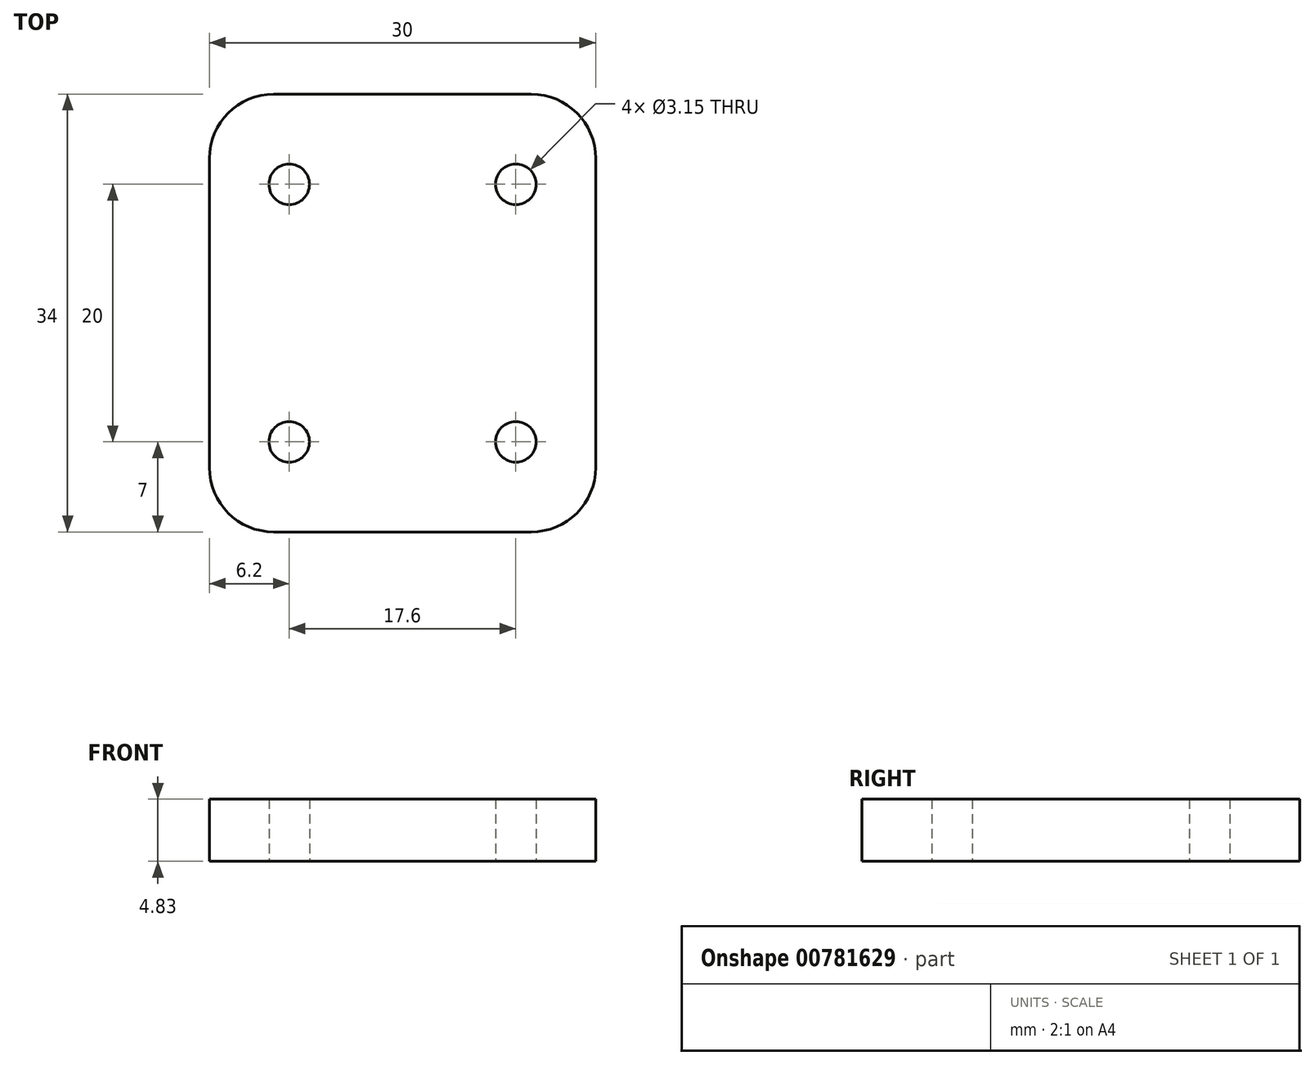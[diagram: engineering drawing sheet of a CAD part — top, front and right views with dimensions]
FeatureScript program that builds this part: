
annotation { "Feature Type Name" : "Feature", "Feature Type Description" : "" }
export const myFeature = defineFeature(function(context is Context, id is Id, definition is map)
    precondition{}
    {
        {
            var Q0;
            Q0=qCreatedBy(makeId("Top.planeOp"),FACE);
            var sketch = newSketch(context, id + "F0", { "sketchPlane" : qUnion([Q0])});
            skCircle(sketch, "E0", {"center": v(-8.8, -10) * mm, "radius": 1.57 * mm});
            skCircle(sketch, "E1", {"center": v(8.8, -10) * mm, "radius": 1.57 * mm});
            skLineSegment(sketch, "E2", {"start": v(-8.8, -10) * mm, "end": v(8.8, -10) * mm, "construction": true});
            skPoint(sketch, "E3.positionSnap0", {"position": v(0, -10) * mm});
            skCircle(sketch, "E4", {"center": v(-8.8, -10) * mm, "radius": 2.3 * mm, "construction": true});
            skCircle(sketch, "E5", {"center": v(8.8, -10) * mm, "radius": 2.3 * mm, "construction": true});
            skLineSegment(sketch, "E6.bottom", {"start": v(15, 17) * mm, "end": v(-15, 17) * mm});
            skLineSegment(sketch, "E6.top", {"start": v(15, -17) * mm, "end": v(-15, -17) * mm});
            skLineSegment(sketch, "E6.left", {"start": v(15, 17) * mm, "end": v(15, -17) * mm});
            skLineSegment(sketch, "E6.right", {"start": v(-15, 17) * mm, "end": v(-15, -17) * mm});
            skPoint(sketch, "E6.middle", {"position": v(0, 0) * mm});
            skLineSegment(sketch, "E7", {"start": v(-15, 0) * mm, "end": v(15, 0) * mm, "construction": true});
            skPoint(sketch, "E8.MirrorP", {"position": v(0, 10) * mm});
            skLineSegment(sketch, "E9.MirrorCS", {"start": v(-8.8, 10) * mm, "end": v(8.8, 10) * mm, "construction": true});
            skCircle(sketch, "E10.MirrorC", {"center": v(8.8, 10) * mm, "radius": 1.57 * mm});
            skCircle(sketch, "E11.MirrorC", {"center": v(-8.8, 10) * mm, "radius": 2.3 * mm, "construction": true});
            skCircle(sketch, "E12.MirrorC", {"center": v(8.8, 10) * mm, "radius": 2.3 * mm, "construction": true});
            skCircle(sketch, "E13.MirrorC", {"center": v(-8.8, 10) * mm, "radius": 1.57 * mm});
            skLineSegment(sketch, "E14", {"start": v(0, 10) * mm, "end": v(0, -10) * mm, "construction": true});
            skSolve(sketch);
        }
        {
            var Q0;
            Q0 = qSketchRegion(id + "F0", true);
            extrude(context, id + "F1", {"entities" : qUnion([Q0]), "depth" : 4.83 * mm, "offsetDistance" : 25 * mm});
        }
        {
            var Q0;
            Q0=makeQuery(id+"F1.opExtrude","SWEPT_EDGE",EDGE,{"disambiguationData":[OSD([sQuery(id+"F0.wireOp",EDGE,"E6.top"),sQuery(id+"F0.wireOp",EDGE,"E6.right")])]});
            var Q1;
            Q1=makeQuery(id+"F1.opExtrude","SWEPT_EDGE",EDGE,{"disambiguationData":[OSD([sQuery(id+"F0.wireOp",EDGE,"E6.top"),sQuery(id+"F0.wireOp",EDGE,"E6.left")])]});
            var Q2;
            Q2=makeQuery(id+"F1.opExtrude","SWEPT_EDGE",EDGE,{"disambiguationData":[OSD([sQuery(id+"F0.wireOp",EDGE,"E6.bottom"),sQuery(id+"F0.wireOp",EDGE,"E6.right")])]});
            var Q3;
            Q3=makeQuery(id+"F1.opExtrude","SWEPT_EDGE",EDGE,{"disambiguationData":[OSD([sQuery(id+"F0.wireOp",EDGE,"E6.bottom"),sQuery(id+"F0.wireOp",EDGE,"E6.left")])]});
            fillet(context, id + "F2", {"entities" : qUnion([Q0, Q1, Q2, Q3]), "radius" : 5 * mm, "tangentPropagation" : true, "allowEdgeOverflow" : false});
        }
    });
